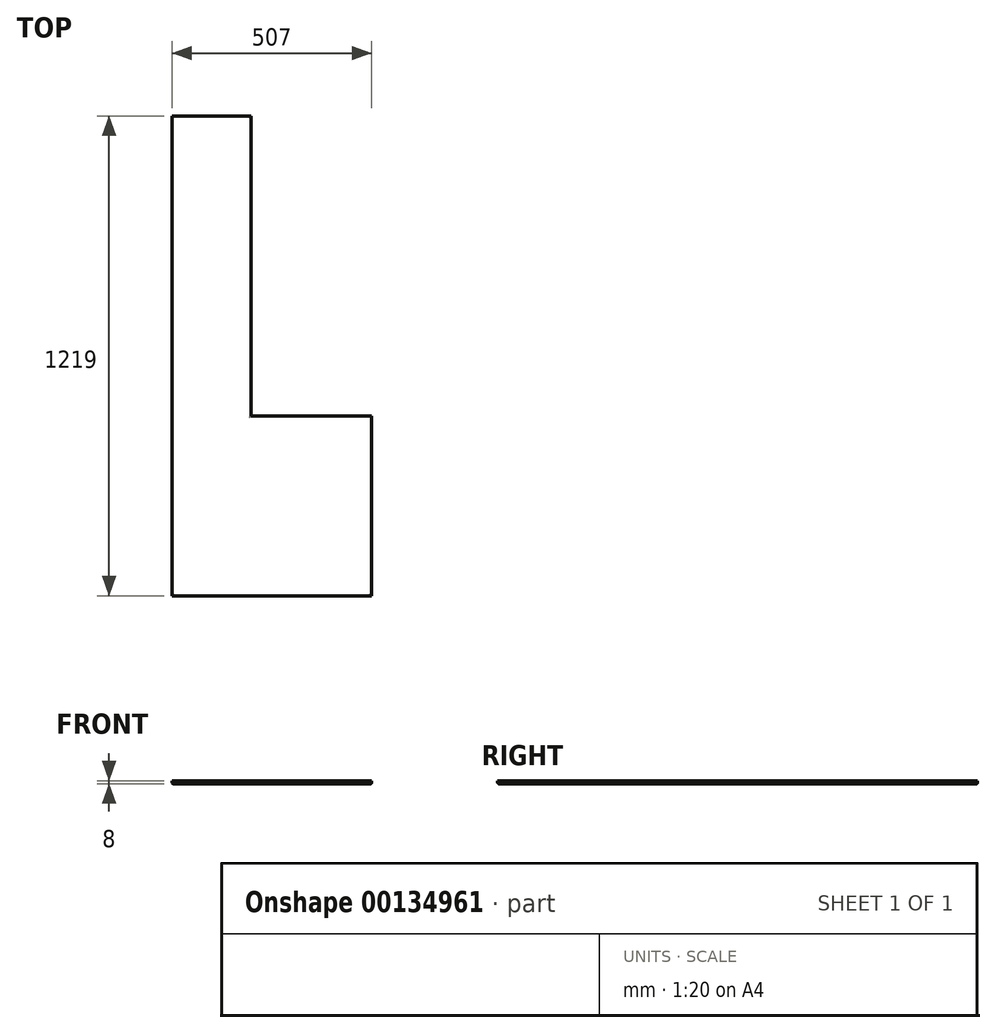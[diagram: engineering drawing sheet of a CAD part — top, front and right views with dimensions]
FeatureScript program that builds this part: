
annotation { "Feature Type Name" : "Feature", "Feature Type Description" : "" }
export const myFeature = defineFeature(function(context is Context, id is Id, definition is map)
    precondition{}
    {
        {
            var Q0;
            Q0=qCreatedBy(makeId("Top.planeOp"),FACE);
            var sketch = newSketch(context, id + "F0", { "sketchPlane" : qUnion([Q0])});
            skLineSegment(sketch, "E0", {"start": v(0, 0) * mm, "end": v(507, 0) * mm});
            skLineSegment(sketch, "E1", {"start": v(507, 0) * mm, "end": v(507, 457) * mm});
            skLineSegment(sketch, "E2", {"start": v(507, 457) * mm, "end": v(200, 457) * mm});
            skLineSegment(sketch, "E3", {"start": v(200, 457) * mm, "end": v(200, 1219) * mm});
            skLineSegment(sketch, "E4", {"start": v(200, 1219) * mm, "end": v(0, 1219) * mm});
            skLineSegment(sketch, "E5", {"start": v(0, 1219) * mm, "end": v(0, 0) * mm});
            skSolve(sketch);
        }
        {
            var Q0;
            Q0=makeQuery(id+"F0.imprint","IMPRINT",FACE,{"disambiguationData":[TD([[makeQuery(id+"F0.imprint","IMPRINT",EDGE,{"derivedFrom":sQuery(id+"F0.wireOp",EDGE,"E0")}),1.0]])]});
            extrude(context, id + "F1", {"entities" : qUnion([Q0]), "depth" : 8 * mm});
        }
        {
            var Q0;
            Q0=makeQuery(id+"F1.opExtrude","CAP_FACE",FACE,{"disambiguationData":[OSD([sQuery(id+"F0.wireOp",EDGE,"E0"),sQuery(id+"F0.wireOp",EDGE,"E1"),sQuery(id+"F0.wireOp",EDGE,"E2"),sQuery(id+"F0.wireOp",EDGE,"E3"),sQuery(id+"F0.wireOp",EDGE,"E4"),sQuery(id+"F0.wireOp",EDGE,"E5")])],"isStart":true});
            fillet(context, id + "F2", {"entities" : qUnion([Q0]), "radius" : 4 * mm, "tangentPropagation" : true, "allowEdgeOverflow" : false});
        }
    });
